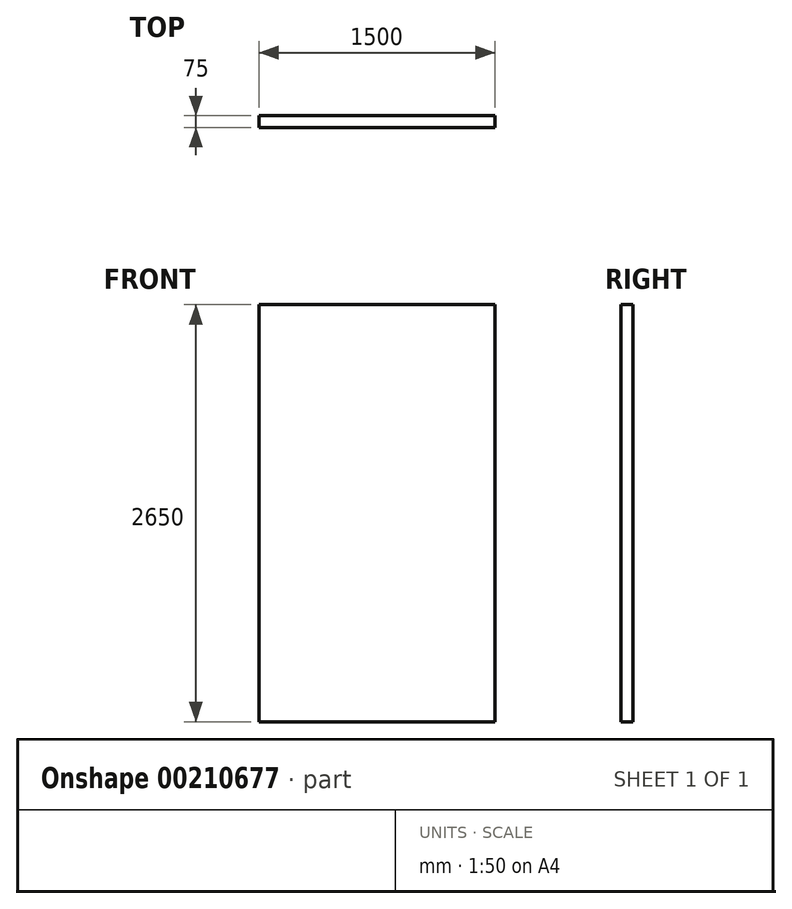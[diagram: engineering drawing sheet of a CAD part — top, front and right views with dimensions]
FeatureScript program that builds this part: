
annotation { "Feature Type Name" : "Feature", "Feature Type Description" : "" }
export const myFeature = defineFeature(function(context is Context, id is Id, definition is map)
    precondition{}
    {
        {
            var Q0;
            Q0=qCreatedBy(makeId("Front.planeOp"),FACE);
            var sketch = newSketch(context, id + "F0", { "sketchPlane" : qUnion([Q0])});
            skLineSegment(sketch, "E0.bottom", {"start": v(0, 0) * mm, "end": v(1500, 0) * mm});
            skLineSegment(sketch, "E0.top", {"start": v(0, 2650) * mm, "end": v(1500, 2650) * mm});
            skLineSegment(sketch, "E0.left", {"start": v(0, 0) * mm, "end": v(0, 2650) * mm});
            skLineSegment(sketch, "E0.right", {"start": v(1500, 0) * mm, "end": v(1500, 2650) * mm});
            skSolve(sketch);
        }
        {
            var Q0;
            Q0=makeQuery(id+"F0.imprint","IMPRINT",FACE,{"disambiguationData":[TD([[makeQuery(id+"F0.imprint","IMPRINT",EDGE,{"derivedFrom":sQuery(id+"F0.wireOp",EDGE,"E0.bottom")}),1.0]])]});
            extrude(context, id + "F1", {"entities" : qUnion([Q0]), "depth" : 75 * mm});
        }
    });
